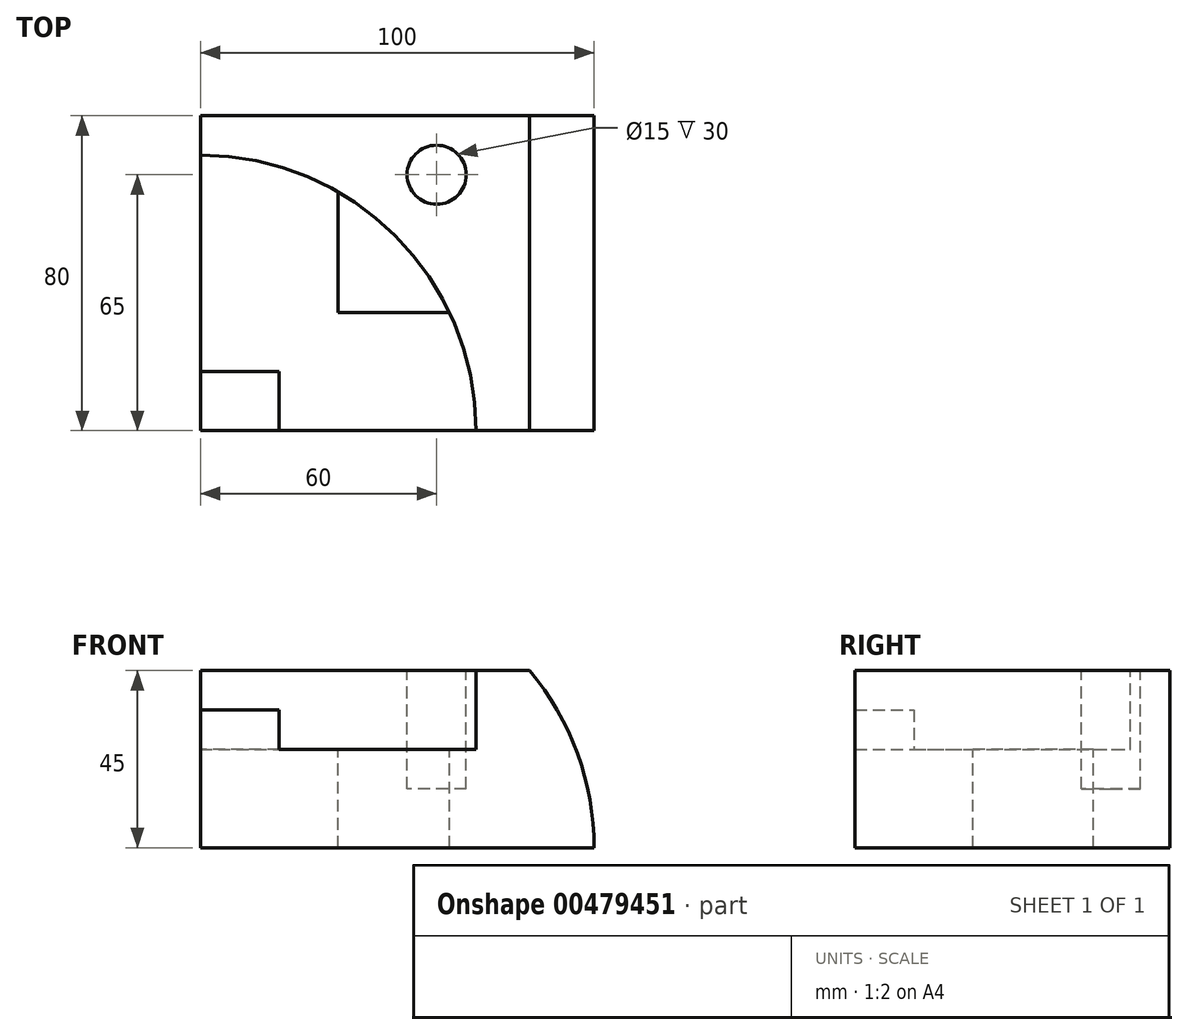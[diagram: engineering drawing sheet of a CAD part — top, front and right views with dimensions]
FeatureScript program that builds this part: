
annotation { "Feature Type Name" : "Feature", "Feature Type Description" : "" }
export const myFeature = defineFeature(function(context is Context, id is Id, definition is map)
    precondition{}
    {
        {
            var Q0;
            Q0=qCreatedBy(makeId("Top.planeOp"),FACE);
            var sketch = newSketch(context, id + "F0", { "sketchPlane" : qUnion([Q0])});
            skLineSegment(sketch, "E0.bottom", {"start": v(0, 0) * mm, "end": v(100, 0) * mm});
            skLineSegment(sketch, "E0.top", {"start": v(0, 80) * mm, "end": v(100, 80) * mm});
            skLineSegment(sketch, "E0.left", {"start": v(0, 0) * mm, "end": v(0, 80) * mm});
            skLineSegment(sketch, "E0.right", {"start": v(100, 0) * mm, "end": v(100, 80) * mm});
            skSolve(sketch);
        }
        {
            var Q0;
            Q0 = qSketchRegion(id + "F0", true);
            extrude(context, id + "F1", {"entities" : qUnion([Q0]), "depth" : 45 * mm});
        }
        {
            var Q0;
            Q0=makeQuery(id+"F1.opExtrude","CAP_FACE",FACE,{"disambiguationData":[OSD([sQuery(id+"F0.wireOp",EDGE,"E0.bottom"),sQuery(id+"F0.wireOp",EDGE,"E0.top"),sQuery(id+"F0.wireOp",EDGE,"E0.left"),sQuery(id+"F0.wireOp",EDGE,"E0.right")])],"isStart":false});
            var sketch = newSketch(context, id + "F2", { "sketchPlane" : qUnion([Q0])});
            skCircle(sketch, "E1", {"center": v(0, 0) * mm, "radius": 70 * mm});
            skSolve(sketch);
        }
        {
            var Q0;
            Q0 = qSketchRegion(id + "F2", true);
            extrude(context, id + "F3", {"entities" : qUnion([Q0]), "operationType" : NewBodyOperationType.REMOVE, "oppositeDirection" : true, "depth" : 20 * mm});
        }
        {
            var Q0;
            Q0=makeQuery(id+"F3.boolean.opBoolean","COPY",FACE,{"derivedFrom":makeQuery(id+"F3.opExtrude","CAP_FACE",FACE,{"disambiguationData":[OSD([sQuery(id+"F2.wireOp",EDGE,"E1")])],"isStart":false})});
            var sketch = newSketch(context, id + "F4", { "sketchPlane" : qUnion([Q0])});
            skLineSegment(sketch, "E2", {"start": v(35, 60.62) * mm, "end": v(35, 30) * mm});
            skLineSegment(sketch, "E3", {"start": v(35, 30) * mm, "end": v(63.25, 30) * mm});
            skSolve(sketch);
        }
        {
            var Q0;
            Q0 = qSketchRegion(id + "F4", true);
            var Q1;
            {var subQ0=sQuery(id+"F4.wireOp",EDGE,"E2");Q1=makeQuery(id+"F4.imprint","IMPRINT",FACE,{"disambiguationData":[TD([[makeQuery(id+"F4.imprint","IMPRINT",EDGE,{"derivedFrom":subQ0}),1.0]])]});}
            extrude(context, id + "F5", {"entities" : qUnion([Q0, Q1]), "operationType" : NewBodyOperationType.REMOVE, "endBound" : BoundingType.THROUGH_ALL, "oppositeDirection" : true, "depth" : 25 * mm});
        }
        {
            var Q0;
            Q0=makeQuery(id+"F3.boolean.opBoolean","COPY",FACE,{"derivedFrom":makeQuery(id+"F3.opExtrude","CAP_FACE",FACE,{"disambiguationData":[OSD([sQuery(id+"F2.wireOp",EDGE,"E1")])],"isStart":false})});
            var sketch = newSketch(context, id + "F6", { "sketchPlane" : qUnion([Q0])});
            skLineSegment(sketch, "E4.bottom", {"start": v(0, 0) * mm, "end": v(20, 0) * mm});
            skLineSegment(sketch, "E4.top", {"start": v(0, 15) * mm, "end": v(20, 15) * mm});
            skLineSegment(sketch, "E4.left", {"start": v(0, 0) * mm, "end": v(0, 15) * mm});
            skLineSegment(sketch, "E4.right", {"start": v(20, 0) * mm, "end": v(20, 15) * mm});
            skSolve(sketch);
        }
        {
            var Q0;
            Q0 = qSketchRegion(id + "F6", true);
            extrude(context, id + "F7", {"entities" : qUnion([Q0]), "operationType" : NewBodyOperationType.ADD, "depth" : 10 * mm});
        }
        {
            var Q0;
            Q0=makeQuery(id+"F1.opExtrude","CAP_FACE",FACE,{"disambiguationData":[OSD([sQuery(id+"F0.wireOp",EDGE,"E0.bottom"),sQuery(id+"F0.wireOp",EDGE,"E0.top"),sQuery(id+"F0.wireOp",EDGE,"E0.left"),sQuery(id+"F0.wireOp",EDGE,"E0.right")])],"isStart":false});
            var sketch = newSketch(context, id + "F8", { "sketchPlane" : qUnion([Q0])});
            skCircle(sketch, "E5", {"center": v(60, 65) * mm, "radius": 7.5 * mm});
            skSolve(sketch);
        }
        {
            var Q0;
            Q0 = qSketchRegion(id + "F8", true);
            extrude(context, id + "F9", {"entities" : qUnion([Q0]), "operationType" : NewBodyOperationType.REMOVE, "oppositeDirection" : true, "depth" : 30 * mm});
        }
        {
            var Q0;
            Q0=makeQuery(id+"F7.boolean.opBoolean","MERGE",FACE,{"derivedFrom":[makeQuery(id+"F1.opExtrude","SWEPT_FACE",FACE,{"disambiguationData":[OSD([sQuery(id+"F0.wireOp",EDGE,"E0.bottom")])]}),makeQuery(id+"F7.opExtrude","SWEPT_FACE",FACE,{"disambiguationData":[OSD([sQuery(id+"F6.wireOp",EDGE,"E4.bottom")])]})]});
            var sketch = newSketch(context, id + "F10", { "sketchPlane" : qUnion([Q0])});
            skSolve(sketch);
        }
        {
            var Q0;
            {var subQ1=sQuery(id+"F0.wireOp",EDGE,"E0.bottom");Q0=makeQuery(id+"F10.imprint","IMPRINT",FACE,{"disambiguationData":[TD([[makeQuery(id+"F10.imprint","IMPRINT",EDGE,{"derivedFrom":makeQuery(id+"F1.opExtrude","CAP_EDGE",EDGE,{"disambiguationData":[OSD([subQ1])],"isStart":true})}),1.0]])]});}
            var sketch = newSketch(context, id + "F11", { "sketchPlane" : qUnion([Q0])});
            skArc(sketch, "E6", {"start": v(100, 0) * mm, "mid": v(95.78, 23.94) * mm, "end": v(83.62, 45) * mm});
            skLineSegment(sketch, "E7", {"start": v(83.62, 45) * mm, "end": v(100, 45) * mm});
            skLineSegment(sketch, "E8", {"start": v(100, 45) * mm, "end": v(100, 0) * mm});
            skSolve(sketch);
        }
        {
            var Q0;
            Q0 = qSketchRegion(id + "F11", true);
            extrude(context, id + "F12", {"entities" : qUnion([Q0]), "operationType" : NewBodyOperationType.REMOVE, "endBound" : BoundingType.THROUGH_ALL, "oppositeDirection" : true, "depth" : 25 * mm});
        }
    });
